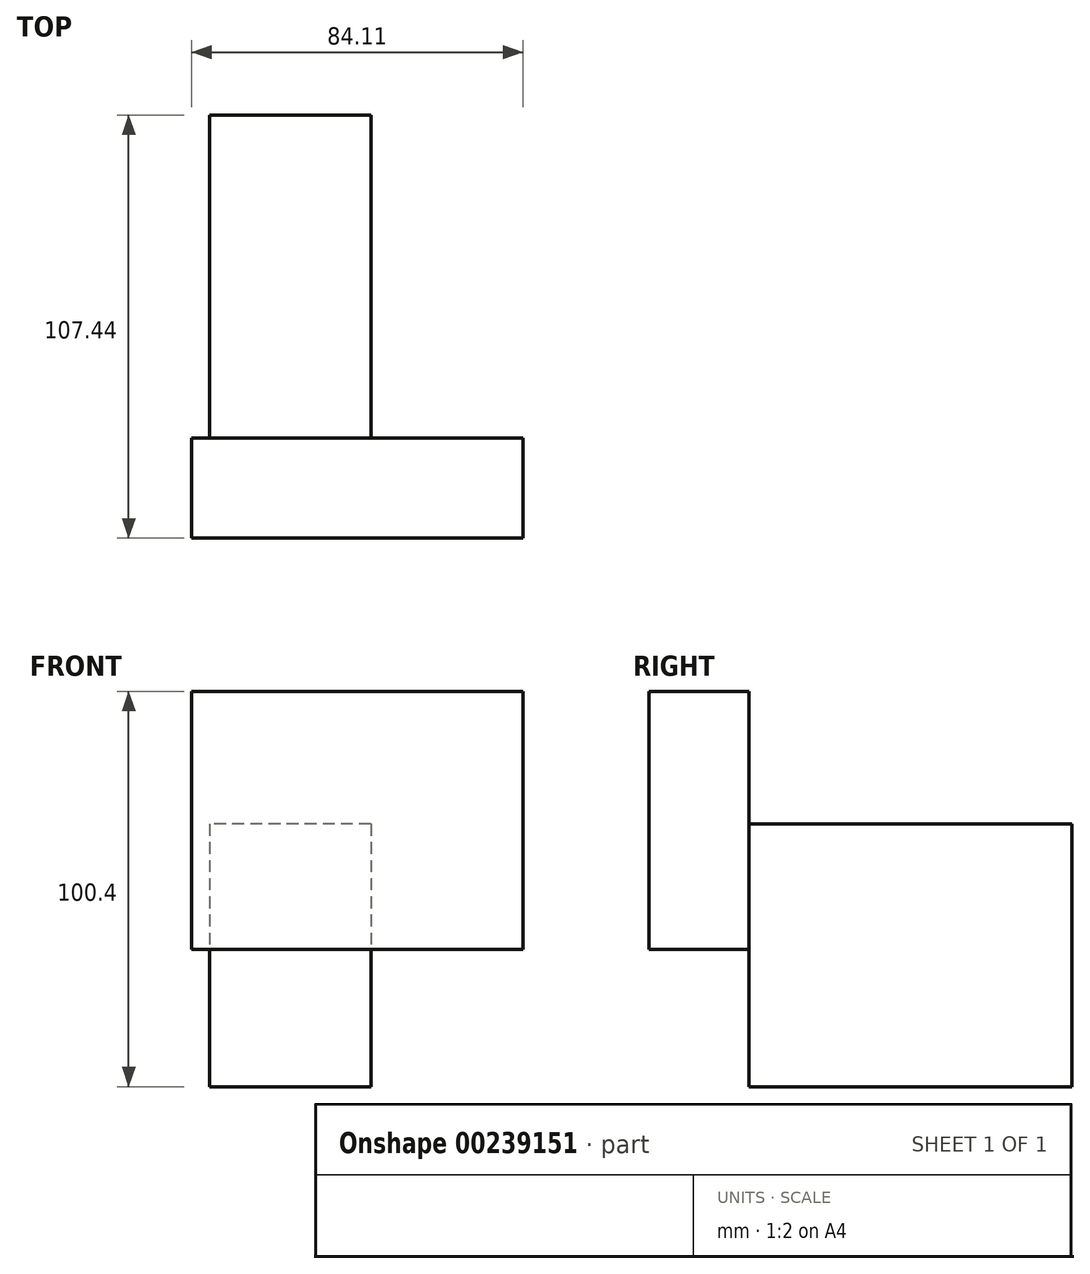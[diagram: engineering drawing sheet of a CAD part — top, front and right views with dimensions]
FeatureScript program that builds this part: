
annotation { "Feature Type Name" : "Feature", "Feature Type Description" : "" }
export const myFeature = defineFeature(function(context is Context, id is Id, definition is map)
    precondition{}
    {
        {
            var Q0;
            Q0=qCreatedBy(makeId("Front.planeOp"),FACE);
            var sketch = newSketch(context, id + "F0", { "sketchPlane" : qUnion([Q0])});
            skLineSegment(sketch, "E0.bottom", {"start": v(38.61, 33.67) * mm, "end": v(-45.5, 33.67) * mm});
            skLineSegment(sketch, "E0.top", {"start": v(38.61, -31.88) * mm, "end": v(-45.5, -31.88) * mm});
            skLineSegment(sketch, "E0.left", {"start": v(38.61, 33.67) * mm, "end": v(38.61, -31.88) * mm});
            skLineSegment(sketch, "E0.right", {"start": v(-45.5, 33.67) * mm, "end": v(-45.5, -31.88) * mm});
            skSolve(sketch);
        }
        {
            var Q0;
            Q0 = qSketchRegion(id + "F0", true);
            extrude(context, id + "F1", {"entities" : qUnion([Q0]), "depth" : 25.4 * mm});
        }
        {
            var Q0;
            Q0=makeQuery(id+"F1.opExtrude","CAP_FACE",FACE,{"disambiguationData":[OSD([sQuery(id+"F0.wireOp",EDGE,"E0.bottom"),sQuery(id+"F0.wireOp",EDGE,"E0.top"),sQuery(id+"F0.wireOp",EDGE,"E0.left"),sQuery(id+"F0.wireOp",EDGE,"E0.right")])],"isStart":true});
            var sketch = newSketch(context, id + "F2", { "sketchPlane" : qUnion([Q0])});
            skLineSegment(sketch, "E1.bottom", {"start": v(0, 0) * mm, "end": v(40.94, 0) * mm});
            skLineSegment(sketch, "E1.top", {"start": v(0, -66.73) * mm, "end": v(40.94, -66.73) * mm});
            skLineSegment(sketch, "E1.left", {"start": v(0, 0) * mm, "end": v(0, -66.73) * mm});
            skLineSegment(sketch, "E1.right", {"start": v(40.94, 0) * mm, "end": v(40.94, -66.73) * mm});
            skSolve(sketch);
        }
        {
            var Q0;
            Q0 = qSketchRegion(id + "F2", true);
            extrude(context, id + "F3", {"entities" : qUnion([Q0]), "operationType" : NewBodyOperationType.ADD, "depth" : 82.04 * mm});
        }
    });
